# Revit family: Rectangular_basin
name_source: partatom
category: Furniture
units: mm (PartAtom-declared; Revit-internal decimal feet)

## family parameters
Always vertical = Yes
Cut with Voids When Loaded = No
OmniClass Number = 23.40.20.00
OmniClass Title = General Furniture and Specialties
Room Calculation Point = No
Shared = No
Work Plane-Based = No

## types (6) — shared parameters
Manufacturer = Hafa Bathroom Group AB
Material finish = Porcelain
URL = www.hafa.se

## per-type parameters (varying)
| type | Article number | Back to bowl | Back to tap hole | Back to waste hole | Basin depth | Bowl depth | Bowl inner width | GTIN | Model | Width basin |
| Rektangular basin Compact 600 | 1273208 | 115 mm  [stored 0.377297 ft] | 60 mm  [stored 0.19685 ft] | 220 mm  [stored 0.721785 ft] | 395 mm  [stored 1.29593 ft] | 225 mm  [stored 0.738189 ft] | 440 mm  [stored 1.44357 ft] | 7330027092638 | Rektangular ho 600 compact | 610 mm  [stored 2.00131 ft] |
| Rectangular basin Compact 800 | 1273183 | 115 mm  [stored 0.377297 ft] | 60 mm  [stored 0.19685 ft] | 217 mm | 395 mm  [stored 1.29593 ft] | 225 mm  [stored 0.738189 ft] | 440 mm  [stored 1.44357 ft] | 7330027107042 | Rektangular ho compact 800 | 810 mm |
| Rektangular basin 600 | 1273200 | 115 mm  [stored 0.377297 ft] | 55 mm  [stored 0.180446 ft] | 230 mm  [stored 0.754593 ft] | 465 mm  [stored 1.52559 ft] | 275 mm | 440 mm  [stored 1.44357 ft] | 7330027018928 | Rektangular ho 600 | 610 mm  [stored 2.00131 ft] |
| Rektangular basin 800 | 1273180 | 115 mm  [stored 0.377297 ft] | 55 mm  [stored 0.180446 ft] | 220 mm  [stored 0.721785 ft] | 465 mm  [stored 1.52559 ft] | 270 mm  [stored 0.885827 ft] | 480 mm  [stored 1.5748 ft] | 7330027103709 | Rektangular ho 800 | 810 mm |
| Rektangular basin 900 | 1273201 | 115 mm  [stored 0.377297 ft] | 55 mm  [stored 0.180446 ft] | 220 mm  [stored 0.721785 ft] | 465 mm  [stored 1.52559 ft] | 275 mm | 480 mm  [stored 1.5748 ft] | 7330027018935 | Rektangular ho 900 | 910 mm |
| Rektangular basin 1000 | 1273182 | 120 mm  [stored 0.393701 ft] | 55 mm  [stored 0.180446 ft] | 220 mm  [stored 0.721785 ft] | 465 mm  [stored 1.52559 ft] | 265 mm  [stored 0.869423 ft] | 510 mm  [stored 1.67323 ft] | 7330027103716 | Rektangular ho 1000 | 1010 mm  [stored 3.31365 ft] |

note: [stored X ft] marks values corroborated as IEEE doubles in the binary element streams (Revit-internal decimal feet)

## geometry (parser evidence)
native form markers: Sweep x2
no freeform markers — native parametric forms only
